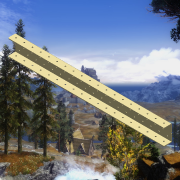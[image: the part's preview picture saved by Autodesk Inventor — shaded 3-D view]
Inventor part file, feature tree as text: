
AUTODESK INVENTOR PART (.ipt)
format: ipt  version: 2015 SP1 (Build 190203100, 203)  size: 576,000 bytes
history: native  units: in
note: dims shown in document units (in); Inventor stores cm internally (conversion verified against a paired STEP export)
features: plane x4, other x2, extrude x1, imported_body x1, sketch x1
ambient origin geometry x8: Origin, YZ Plane, XZ Plane, XY Plane, X Axis, Y Axis, Z Axis, Center Point
bodies: Body1 (feature_tree)
feature tree (9):
  other  "Break-Corner1"
  other  "1 x 2 x 1 x 0.090 C-Channel (59 length)1"
  plane  "Work Plane1"
  extrude  "Extrusion1"  Depth=1.0in TaperAngle=0.0deg
  plane  "Work Plane2"
  plane  "Work Plane3"
  plane  "Work Plane4"
  imported_body  "Base1"
  sketch  "Sketch1"  dims[d0=19.0in d1=1.0in d2=0.0in d7=0.1875in]
